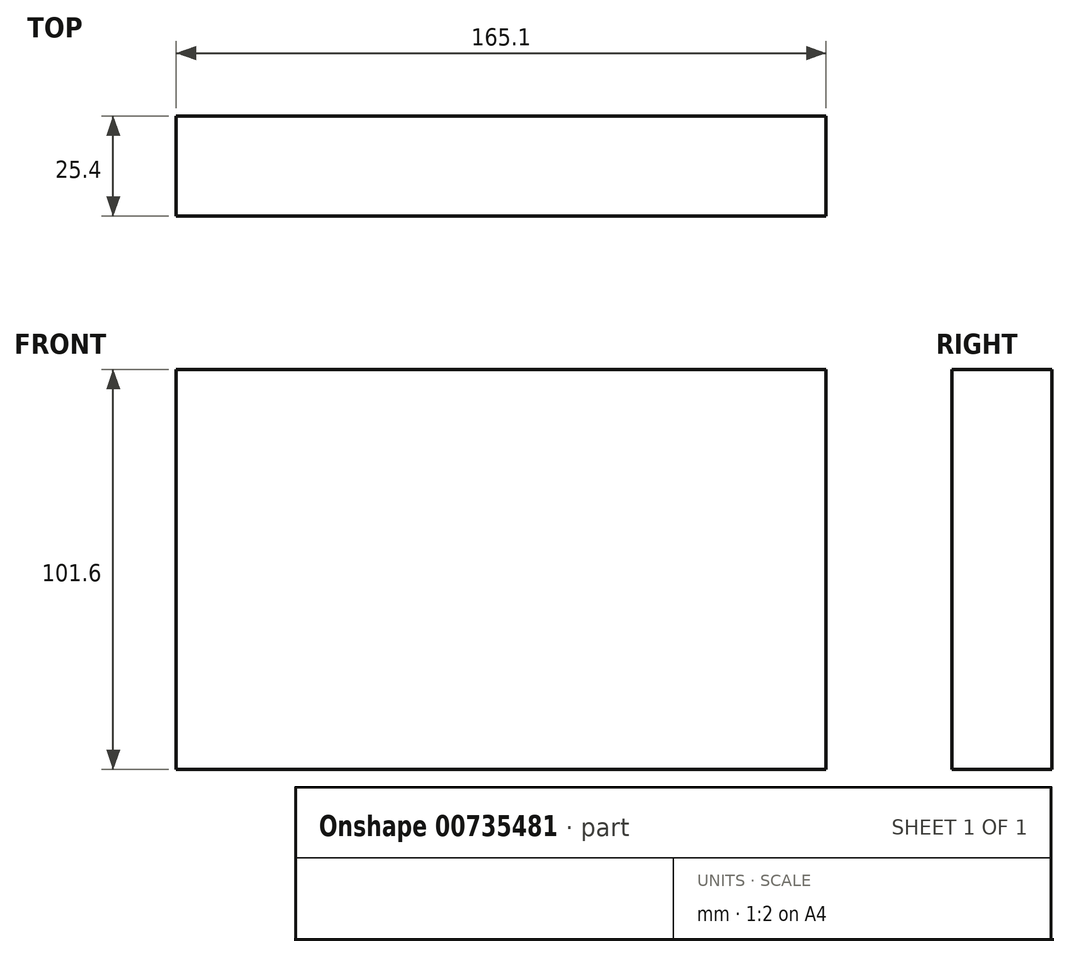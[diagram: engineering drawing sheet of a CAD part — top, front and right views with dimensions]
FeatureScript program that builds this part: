
annotation { "Feature Type Name" : "Feature", "Feature Type Description" : "" }
export const myFeature = defineFeature(function(context is Context, id is Id, definition is map)
    precondition{}
    {
        {
            var Q0;
            Q0=qCreatedBy(makeId("Front.planeOp"),FACE);
            var sketch = newSketch(context, id + "F0", { "sketchPlane" : qUnion([Q0])});
            skLineSegment(sketch, "E0.bottom", {"start": v(-82.55, 50.8) * mm, "end": v(82.55, 50.8) * mm});
            skLineSegment(sketch, "E0.top", {"start": v(-82.55, -50.8) * mm, "end": v(82.55, -50.8) * mm});
            skLineSegment(sketch, "E0.left", {"start": v(-82.55, 50.8) * mm, "end": v(-82.55, -50.8) * mm});
            skLineSegment(sketch, "E0.right", {"start": v(82.55, 50.8) * mm, "end": v(82.55, -50.8) * mm});
            skPoint(sketch, "E0.middle", {"position": v(0, 0) * mm});
            skSolve(sketch);
        }
        {
            var Q0;
            Q0=makeQuery(id+"F0.imprint","IMPRINT",FACE,{"disambiguationData":[TD([[makeQuery(id+"F0.imprint","IMPRINT",EDGE,{"derivedFrom":sQuery(id+"F0.wireOp",EDGE,"E0.bottom")}),-1.0]])]});
            extrude(context, id + "F1", {"entities" : qUnion([Q0]), "depth" : 25.4 * mm, "offsetDistance" : 25.4 * mm});
        }
    });
